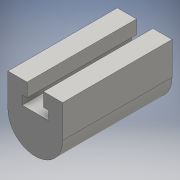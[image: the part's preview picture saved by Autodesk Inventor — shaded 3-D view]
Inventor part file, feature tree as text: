
AUTODESK INVENTOR PART (.ipt)
format: ipt  version: 2016 (Build 200138000, 138)  size: 113,664 bytes
history: native  units: mm
features: extrude x2, sketch x2
ambient origin geometry x8: Origin, YZ Plane, XZ Plane, XY Plane, X Axis, Y Axis, Z Axis, Center Point
bodies: Solid1 (feature_tree)
feature tree (4):
  extrude  "Extrusion1"  Depth=10.0mm
  extrude  "Extrusion2"  Depth=1.5mm
  sketch  "Sketch1"  dims[d0=10.0mm d1=5.0mm]
  sketch  "Sketch2"  dims[d3=2.3876mm d4=1.6002mm d5=2.5mm d6=1.5mm d7=6.0mm d8=5.0mm d9=20.0mm d10=0.0mm d11=3.0mm d12=20.0mm d13=0.0mm]
